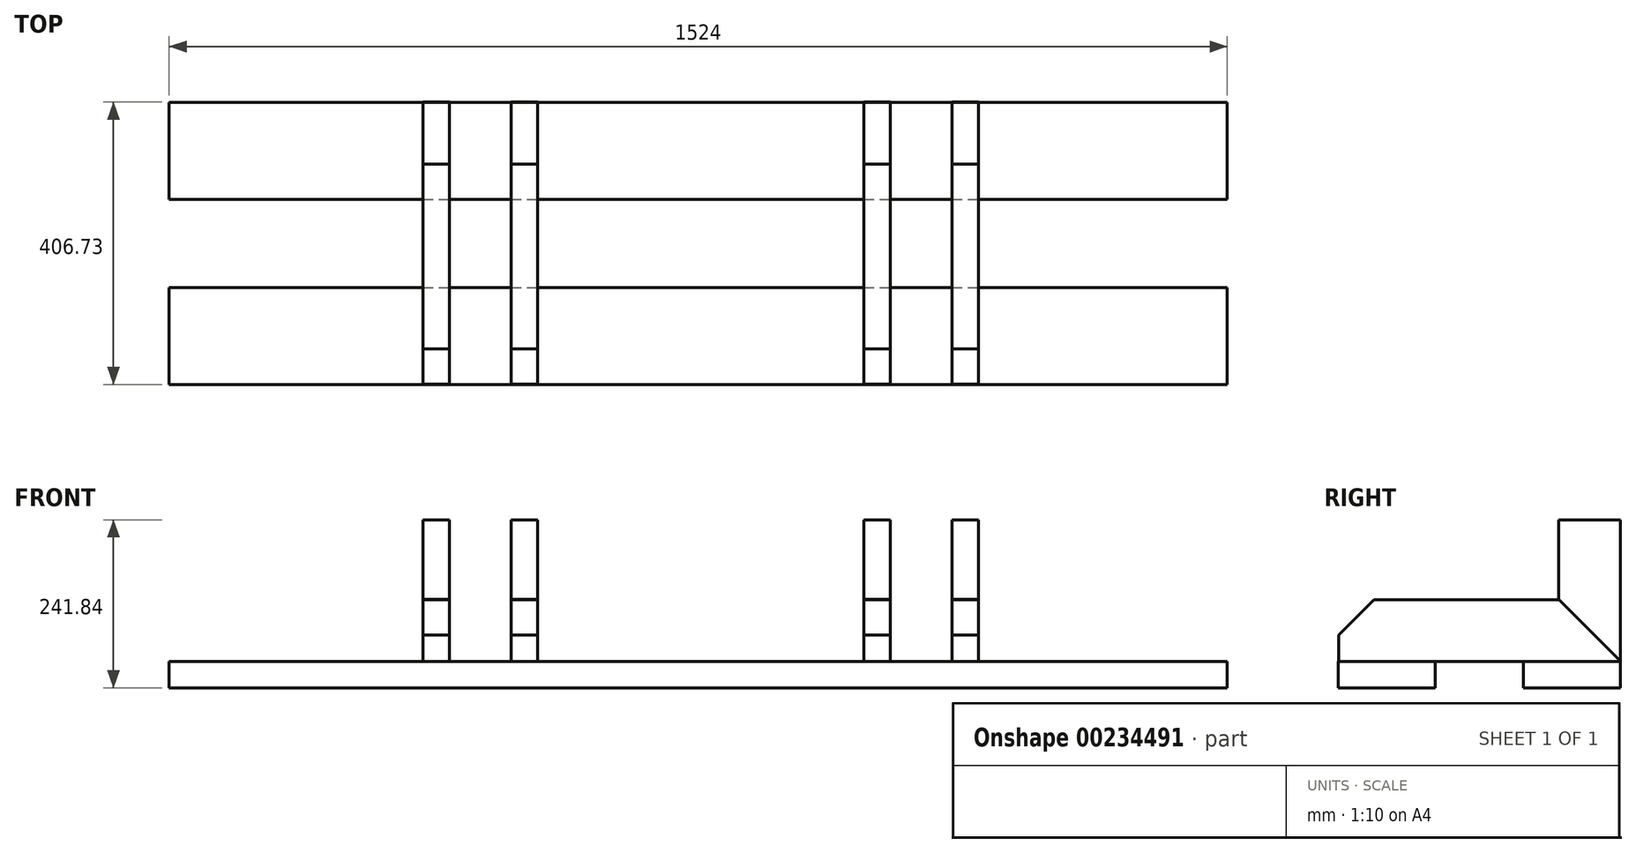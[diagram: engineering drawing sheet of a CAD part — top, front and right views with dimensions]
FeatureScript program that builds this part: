
annotation { "Feature Type Name" : "Feature", "Feature Type Description" : "" }
export const myFeature = defineFeature(function(context is Context, id is Id, definition is map)
    precondition{}
    {
        {
            var Q0;
            Q0=qCreatedBy(makeId("Top.planeOp"),FACE);
            var sketch = newSketch(context, id + "F0", { "sketchPlane" : qUnion([Q0])});
            skLineSegment(sketch, "E0.bottom", {"start": v(-746.5, 102.48) * mm, "end": v(777.5, 102.48) * mm});
            skLineSegment(sketch, "E0.top", {"start": v(-746.5, -37.22) * mm, "end": v(777.5, -37.22) * mm});
            skLineSegment(sketch, "E0.left", {"start": v(-746.5, 102.48) * mm, "end": v(-746.5, -37.22) * mm});
            skLineSegment(sketch, "E0.right", {"start": v(777.5, 102.48) * mm, "end": v(777.5, -37.22) * mm});
            skSolve(sketch);
        }
        {
            var Q0;
            Q0=makeQuery(id+"F0.imprint","IMPRINT",FACE,{"disambiguationData":[TD([[makeQuery(id+"F0.imprint","IMPRINT",EDGE,{"derivedFrom":sQuery(id+"F0.wireOp",EDGE,"E0.bottom")}),-1.0]])]});
            extrude(context, id + "F1", {"entities" : qUnion([Q0]), "depth" : 38.1 * mm});
        }
        {
            var Q0;
            Q0=makeQuery(id+"F1.opExtrude","SWEPT_BODY",BODY,{"disambiguationData":[OSD([sQuery(id+"F0.wireOp",EDGE,"E0.bottom"),sQuery(id+"F0.wireOp",EDGE,"E0.top"),sQuery(id+"F0.wireOp",EDGE,"E0.left"),sQuery(id+"F0.wireOp",EDGE,"E0.right")])]});
            transform(context, id + "F2", {"entities" : qUnion([Q0]), "transformType" : TransformType.TRANSLATION_3D, "dx" : 0 * mm, "dy" : 0 * mm, "dz" : 0 * mm, "makeCopy" : true});
        }
        {
            var Q0;
            Q0=makeQuery(id+"F2.opPattern","COPY",BODY,{"derivedFrom":makeQuery(id+"F1.opExtrude","SWEPT_BODY",BODY,{"disambiguationData":[OSD([sQuery(id+"F0.wireOp",EDGE,"E0.bottom"),sQuery(id+"F0.wireOp",EDGE,"E0.top"),sQuery(id+"F0.wireOp",EDGE,"E0.left"),sQuery(id+"F0.wireOp",EDGE,"E0.right")])]}),"instanceName":"1"});
            transform(context, id + "F3", {"entities" : qUnion([Q0]), "transformType" : TransformType.TRANSLATION_3D, "dx" : 0 * mm, "dy" : 203.2 * mm, "dz" : 0 * mm, "makeCopy" : false});
        }
        {
            var Q0;
            Q0=makeQuery(id+"F1.opExtrude","SWEPT_BODY",BODY,{"disambiguationData":[OSD([sQuery(id+"F0.wireOp",EDGE,"E0.bottom"),sQuery(id+"F0.wireOp",EDGE,"E0.top"),sQuery(id+"F0.wireOp",EDGE,"E0.left"),sQuery(id+"F0.wireOp",EDGE,"E0.right")])]});
            transform(context, id + "F4", {"entities" : qUnion([Q0]), "transformType" : TransformType.TRANSLATION_3D, "dx" : 0 * mm, "dy" : -152.4 * mm, "dz" : 0 * mm, "makeCopy" : false});
        }
        {
            var Q0;
            Q0=makeQuery(id+"F2.opPattern","COPY",BODY,{"derivedFrom":makeQuery(id+"F1.opExtrude","SWEPT_BODY",BODY,{"disambiguationData":[OSD([sQuery(id+"F0.wireOp",EDGE,"E0.bottom"),sQuery(id+"F0.wireOp",EDGE,"E0.top"),sQuery(id+"F0.wireOp",EDGE,"E0.left"),sQuery(id+"F0.wireOp",EDGE,"E0.right")])]}),"instanceName":"1"});
            transform(context, id + "F5", {"entities" : qUnion([Q0]), "transformType" : TransformType.TRANSLATION_3D, "dx" : 0 * mm, "dy" : -114.3 * mm, "dz" : 0 * mm, "makeCopy" : false});
        }
        {
            var Q0;
            Q0=qCreatedBy(makeId("Right.planeOp"),FACE);
            var sketch = newSketch(context, id + "F6", { "sketchPlane" : qUnion([Q0])});
            skLineSegment(sketch, "E1.bottom", {"start": v(-193.1, 88.9) * mm, "end": v(213.3, 88.9) * mm});
            skLineSegment(sketch, "E1.top", {"start": v(-193.1, 0) * mm, "end": v(213.3, 0) * mm});
            skLineSegment(sketch, "E1.left", {"start": v(-193.1, 88.9) * mm, "end": v(-193.1, 0) * mm});
            skLineSegment(sketch, "E1.right", {"start": v(213.3, 88.9) * mm, "end": v(213.3, 0) * mm});
            skSolve(sketch);
        }
        {
            var Q0;
            Q0=makeQuery(id+"F6.imprint","IMPRINT",FACE,{"disambiguationData":[TD([[makeQuery(id+"F6.imprint","IMPRINT",EDGE,{"derivedFrom":sQuery(id+"F6.wireOp",EDGE,"E1.bottom")}),-1.0]])]});
            extrude(context, id + "F7", {"entities" : qUnion([Q0]), "depth" : 38.1 * mm});
        }
        {
            var Q0;
            Q0=makeQuery(id+"F7.opExtrude","SWEPT_BODY",BODY,{"disambiguationData":[OSD([sQuery(id+"F6.wireOp",EDGE,"E1.bottom"),sQuery(id+"F6.wireOp",EDGE,"E1.top"),sQuery(id+"F6.wireOp",EDGE,"E1.left"),sQuery(id+"F6.wireOp",EDGE,"E1.right")])]});
            transform(context, id + "F8", {"entities" : qUnion([Q0]), "transformType" : TransformType.TRANSLATION_3D, "dx" : 0 * mm, "dy" : 0 * mm, "dz" : 38.1 * mm, "makeCopy" : false});
        }
        {
            var Q0;
            Q0=makeQuery(id+"F7.opExtrude","SWEPT_EDGE",EDGE,{"disambiguationData":[OSD([sQuery(id+"F6.wireOp",EDGE,"E1.bottom"),sQuery(id+"F6.wireOp",EDGE,"E1.left")])]});
            chamfer(context, id + "F9", {"entities" : qUnion([Q0]), "width" : 50.8 * mm, "tangentPropagation" : true});
        }
        {
            var Q0;
            Q0=makeQuery(id+"F7.opExtrude","SWEPT_EDGE",EDGE,{"disambiguationData":[OSD([sQuery(id+"F6.wireOp",EDGE,"E1.bottom"),sQuery(id+"F6.wireOp",EDGE,"E1.right")])]});
            chamfer(context, id + "F10", {"entities" : qUnion([Q0]), "width" : 88.9 * mm, "tangentPropagation" : true});
        }
        {
            var Q0;
            Q0=makeQuery(id+"F2.opPattern","COPY",BODY,{"derivedFrom":makeQuery(id+"F1.opExtrude","SWEPT_BODY",BODY,{"disambiguationData":[OSD([sQuery(id+"F0.wireOp",EDGE,"E0.bottom"),sQuery(id+"F0.wireOp",EDGE,"E0.top"),sQuery(id+"F0.wireOp",EDGE,"E0.left"),sQuery(id+"F0.wireOp",EDGE,"E0.right")])]}),"instanceName":"1"});
            transform(context, id + "F11", {"entities" : qUnion([Q0]), "transformType" : TransformType.TRANSLATION_3D, "dx" : 0 * mm, "dy" : 21.59 * mm, "dz" : 0 * mm, "makeCopy" : false});
        }
        {
            var Q0;
            Q0=makeQuery(id+"F1.opExtrude","SWEPT_BODY",BODY,{"disambiguationData":[OSD([sQuery(id+"F0.wireOp",EDGE,"E0.bottom"),sQuery(id+"F0.wireOp",EDGE,"E0.top"),sQuery(id+"F0.wireOp",EDGE,"E0.left"),sQuery(id+"F0.wireOp",EDGE,"E0.right")])]});
            transform(context, id + "F12", {"entities" : qUnion([Q0]), "transformType" : TransformType.TRANSLATION_3D, "dx" : 0 * mm, "dy" : -3.8 * mm, "dz" : 0 * mm, "makeCopy" : false});
        }
        {
            var Q0;
            Q0=qCreatedBy(makeId("Right.planeOp"),FACE);
            var sketch = newSketch(context, id + "F13", { "sketchPlane" : qUnion([Q0])});
            skLineSegment(sketch, "E2.bottom", {"start": v(248.89, 98.58) * mm, "end": v(159.99, 98.58) * mm});
            skLineSegment(sketch, "E2.top", {"start": v(248.89, -104.62) * mm, "end": v(159.99, -104.62) * mm});
            skLineSegment(sketch, "E2.left", {"start": v(248.89, 98.58) * mm, "end": v(248.89, -104.62) * mm});
            skLineSegment(sketch, "E2.right", {"start": v(159.99, 98.58) * mm, "end": v(159.99, -104.62) * mm});
            skSolve(sketch);
        }
        {
            var Q0;
            Q0=makeQuery(id+"F13.imprint","IMPRINT",FACE,{"disambiguationData":[TD([[makeQuery(id+"F13.imprint","IMPRINT",EDGE,{"derivedFrom":sQuery(id+"F13.wireOp",EDGE,"E2.bottom")}),1.0]])]});
            extrude(context, id + "F14", {"entities" : qUnion([Q0]), "depth" : 38.1 * mm});
        }
        {
            var Q0;
            Q0=makeQuery(id+"F14.opExtrude","SWEPT_EDGE",EDGE,{"disambiguationData":[OSD([sQuery(id+"F13.wireOp",EDGE,"E2.top"),sQuery(id+"F13.wireOp",EDGE,"E2.right")])]});
            chamfer(context, id + "F15", {"entities" : qUnion([Q0]), "width" : 88.9 * mm, "tangentPropagation" : true});
        }
        {
            var Q0;
            Q0=makeQuery(id+"F14.opExtrude","SWEPT_BODY",BODY,{"disambiguationData":[OSD([sQuery(id+"F13.wireOp",EDGE,"E2.bottom"),sQuery(id+"F13.wireOp",EDGE,"E2.top"),sQuery(id+"F13.wireOp",EDGE,"E2.left"),sQuery(id+"F13.wireOp",EDGE,"E2.right")])]});
            transform(context, id + "F16", {"entities" : qUnion([Q0]), "transformType" : TransformType.TRANSLATION_3D, "dx" : 0 * mm, "dy" : -35.81 * mm, "dz" : 143.26 * mm, "makeCopy" : false});
        }
        {
            var Q0;
            Q0=makeQuery(id+"F7.opExtrude","SWEPT_BODY",BODY,{"disambiguationData":[OSD([sQuery(id+"F6.wireOp",EDGE,"E1.bottom"),sQuery(id+"F6.wireOp",EDGE,"E1.top"),sQuery(id+"F6.wireOp",EDGE,"E1.left"),sQuery(id+"F6.wireOp",EDGE,"E1.right")])]});
            transform(context, id + "F17", {"entities" : qUnion([Q0]), "transformType" : TransformType.TRANSLATION_3D, "dx" : -381 * mm, "dy" : 0 * mm, "dz" : 0 * mm, "makeCopy" : true});
        }
        {
            var Q0;
            Q0=makeQuery(id+"F14.opExtrude","SWEPT_BODY",BODY,{"disambiguationData":[OSD([sQuery(id+"F13.wireOp",EDGE,"E2.bottom"),sQuery(id+"F13.wireOp",EDGE,"E2.top"),sQuery(id+"F13.wireOp",EDGE,"E2.left"),sQuery(id+"F13.wireOp",EDGE,"E2.right")])]});
            transform(context, id + "F18", {"entities" : qUnion([Q0]), "transformType" : TransformType.TRANSLATION_3D, "dx" : -381 * mm, "dy" : 0 * mm, "dz" : 0 * mm, "makeCopy" : true});
        }
        {
            var Q0;
            Q0=makeQuery(id+"F7.opExtrude","SWEPT_BODY",BODY,{"disambiguationData":[OSD([sQuery(id+"F6.wireOp",EDGE,"E1.bottom"),sQuery(id+"F6.wireOp",EDGE,"E1.top"),sQuery(id+"F6.wireOp",EDGE,"E1.left"),sQuery(id+"F6.wireOp",EDGE,"E1.right")])]});
            transform(context, id + "F19", {"entities" : qUnion([Q0]), "transformType" : TransformType.TRANSLATION_3D, "dx" : -254 * mm, "dy" : 0 * mm, "dz" : 0 * mm, "makeCopy" : false});
        }
        {
            var Q0;
            Q0=makeQuery(id+"F14.opExtrude","SWEPT_BODY",BODY,{"disambiguationData":[OSD([sQuery(id+"F13.wireOp",EDGE,"E2.bottom"),sQuery(id+"F13.wireOp",EDGE,"E2.top"),sQuery(id+"F13.wireOp",EDGE,"E2.left"),sQuery(id+"F13.wireOp",EDGE,"E2.right")])]});
            transform(context, id + "F20", {"entities" : qUnion([Q0]), "transformType" : TransformType.TRANSLATION_3D, "dx" : -254 * mm, "dy" : 0 * mm, "dz" : 0 * mm, "makeCopy" : false});
        }
        {
            var Q0;
            Q0=makeQuery(id+"F17.opPattern","COPY",BODY,{"derivedFrom":makeQuery(id+"F7.opExtrude","SWEPT_BODY",BODY,{"disambiguationData":[OSD([sQuery(id+"F6.wireOp",EDGE,"E1.bottom"),sQuery(id+"F6.wireOp",EDGE,"E1.top"),sQuery(id+"F6.wireOp",EDGE,"E1.left"),sQuery(id+"F6.wireOp",EDGE,"E1.right")])]}),"instanceName":"1"});
            transform(context, id + "F21", {"entities" : qUnion([Q0]), "transformType" : TransformType.TRANSLATION_3D, "dx" : 635 * mm, "dy" : 0 * mm, "dz" : 0 * mm, "makeCopy" : true});
        }
        {
            var Q0;
            Q0=makeQuery(id+"F18.opPattern","COPY",BODY,{"derivedFrom":makeQuery(id+"F14.opExtrude","SWEPT_BODY",BODY,{"disambiguationData":[OSD([sQuery(id+"F13.wireOp",EDGE,"E2.bottom"),sQuery(id+"F13.wireOp",EDGE,"E2.top"),sQuery(id+"F13.wireOp",EDGE,"E2.left"),sQuery(id+"F13.wireOp",EDGE,"E2.right")])]}),"instanceName":"1"});
            transform(context, id + "F22", {"entities" : qUnion([Q0]), "transformType" : TransformType.TRANSLATION_3D, "dx" : 635 * mm, "dy" : 0 * mm, "dz" : 0 * mm, "makeCopy" : true});
        }
        {
            var Q0;
            Q0=makeQuery(id+"F7.opExtrude","SWEPT_BODY",BODY,{"disambiguationData":[OSD([sQuery(id+"F6.wireOp",EDGE,"E1.bottom"),sQuery(id+"F6.wireOp",EDGE,"E1.top"),sQuery(id+"F6.wireOp",EDGE,"E1.left"),sQuery(id+"F6.wireOp",EDGE,"E1.right")])]});
            transform(context, id + "F23", {"entities" : qUnion([Q0]), "transformType" : TransformType.TRANSLATION_3D, "dx" : 635 * mm, "dy" : 0 * mm, "dz" : 0 * mm, "makeCopy" : true});
        }
        {
            var Q0;
            Q0=makeQuery(id+"F14.opExtrude","SWEPT_BODY",BODY,{"disambiguationData":[OSD([sQuery(id+"F13.wireOp",EDGE,"E2.bottom"),sQuery(id+"F13.wireOp",EDGE,"E2.top"),sQuery(id+"F13.wireOp",EDGE,"E2.left"),sQuery(id+"F13.wireOp",EDGE,"E2.right")])]});
            transform(context, id + "F24", {"entities" : qUnion([Q0]), "transformType" : TransformType.TRANSLATION_3D, "dx" : 635 * mm, "dy" : 0 * mm, "dz" : 0 * mm, "makeCopy" : true});
        }
    });
